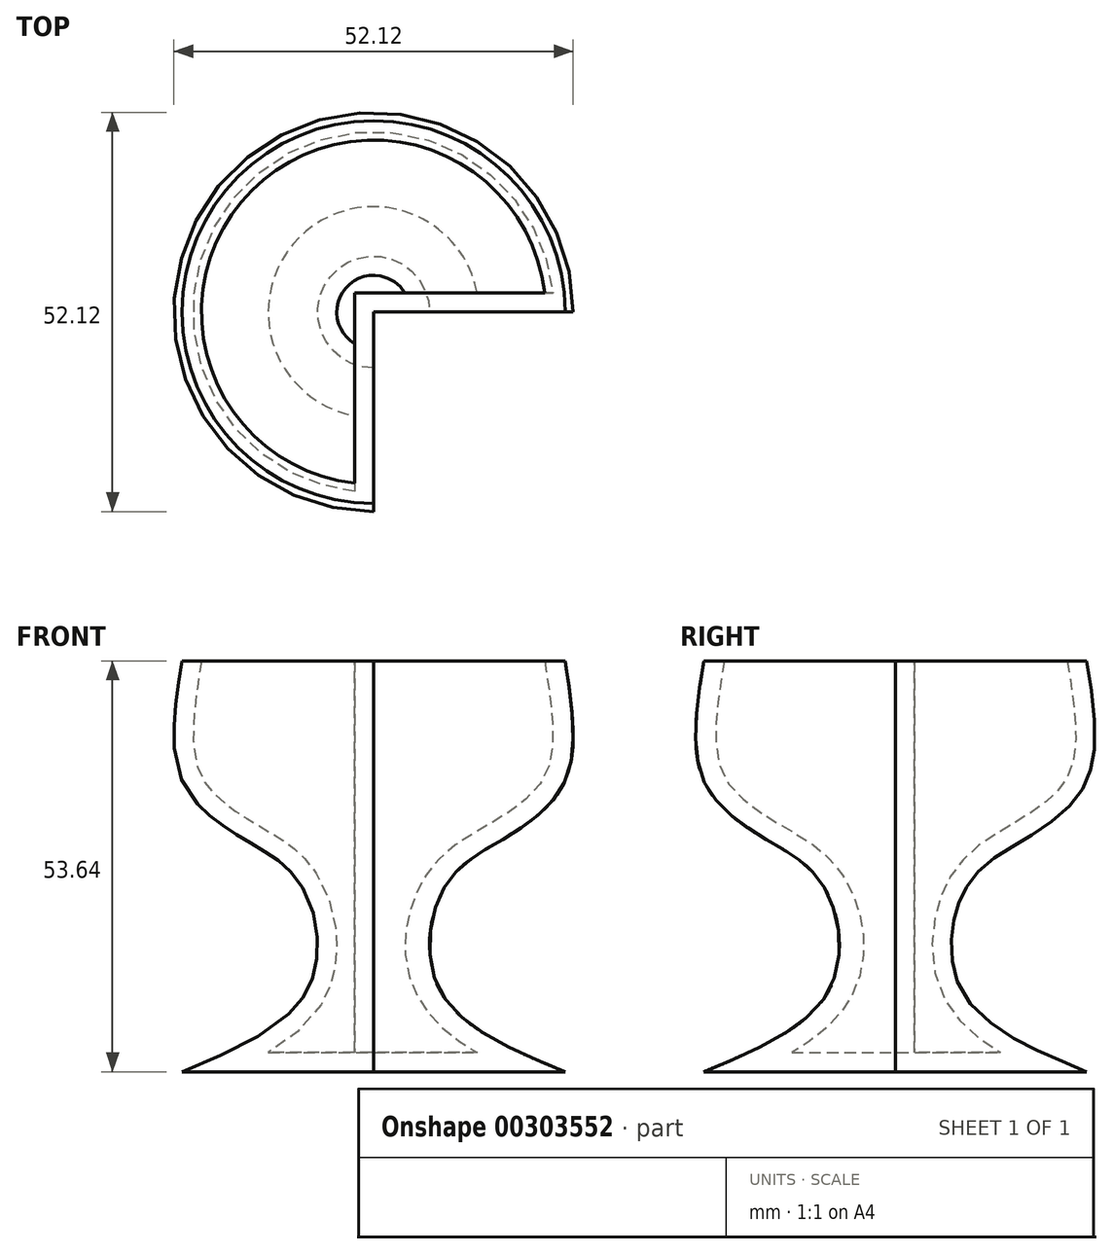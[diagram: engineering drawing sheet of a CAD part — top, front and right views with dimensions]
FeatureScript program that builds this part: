
annotation { "Feature Type Name" : "Feature", "Feature Type Description" : "" }
export const myFeature = defineFeature(function(context is Context, id is Id, definition is map)
    precondition{}
    {
        {
            var Q0;
            Q0=qCreatedBy(makeId("Front.planeOp"),FACE);
            var sketch = newSketch(context, id + "F0", { "sketchPlane" : qUnion([Q0])});
            skLineSegment(sketch, "E0", {"start": v(25, 0) * mm, "end": v(0, 0) * mm});
            skLineSegment(sketch, "E1", {"start": v(0, 0) * mm, "end": v(0, 53.64) * mm});
            skLineSegment(sketch, "E2", {"start": v(0, 53.64) * mm, "end": v(25, 53.64) * mm});
            skFitSpline(sketch, "E3", {"points": [v(25, 53.64) * mm, v(25, 38) * mm, v(16.6, 30.2) * mm, v(9.3, 24.15) * mm, v(8.55, 10.82) * mm, v(25, 0) * mm], "startDerivative": vector(12.91, -80.81) * mm, "endDerivative": vector(86.74, -35.94) * mm});
            skSolve(sketch);
        }
        {
            var Q0;
            Q0=makeQuery(id+"F0.imprint","IMPRINT",FACE,{"disambiguationData":[TD([[makeQuery(id+"F0.imprint","IMPRINT",EDGE,{"derivedFrom":sQuery(id+"F0.wireOp",EDGE,"E0")}),-1.0]])]});
            var Q1;
            Q1=sQuery(id+"F0.wireOp",EDGE,"E1");
            revolve(context, id + "F1", {"entities" : qUnion([Q0]), "axis" : qUnion([Q1]), "revolveType" : RevolveType.ONE_DIRECTION, "angle" : 270 * degree});
        }
        {
            var Q0;
            Q0=makeQuery(id+"F1.opRevolve","SWEPT_FACE",FACE,{"disambiguationData":[OSD([sQuery(id+"F0.wireOp",EDGE,"E2")])]});
            shell(context, id + "F2", {"entities" : qUnion([Q0]), "thickness" : 2.5 * mm});
        }
    });
